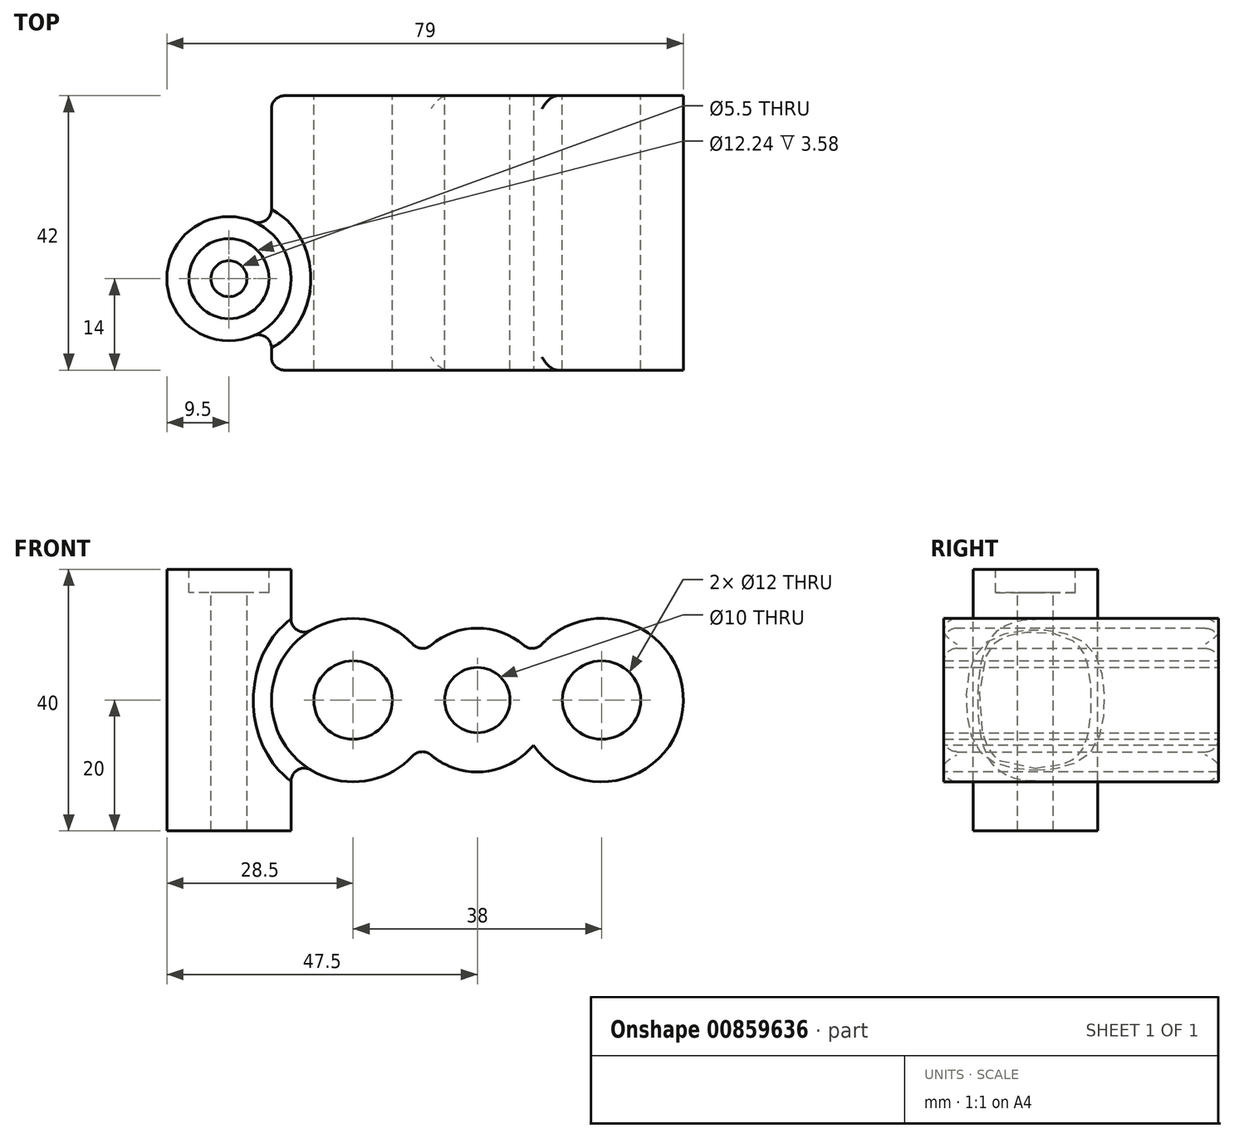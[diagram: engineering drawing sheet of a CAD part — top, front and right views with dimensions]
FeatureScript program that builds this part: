
annotation { "Feature Type Name" : "Feature", "Feature Type Description" : "" }
export const myFeature = defineFeature(function(context is Context, id is Id, definition is map)
    precondition{}
    {
        {
            var Q0;
            Q0=qCreatedBy(makeId("Top.planeOp"),FACE);
            var sketch = newSketch(context, id + "F0", { "sketchPlane" : qUnion([Q0])});
            skCircle(sketch, "E0", {"center": v(0, 0) * mm, "radius": 9.5 * mm});
            skSolve(sketch);
        }
        {
            var Q0;
            Q0 = qSketchRegion(id + "F0", true);
            extrude(context, id + "F1", {"entities" : qUnion([Q0]), "endBound" : BoundingType.SYMMETRIC, "oppositeDirection" : true, "depth" : 40 * mm, "offsetDistance" : 25 * mm});
        }
        {
            var Q0;
            Q0=qCreatedBy(makeId("Front.planeOp"),FACE);
            var sketch = newSketch(context, id + "F2", { "sketchPlane" : qUnion([Q0])});
            skArc(sketch, "E1", {"start": v(29.43, 6.9) * mm, "mid": v(6.5, 0) * mm, "end": v(29.43, -6.9) * mm});
            skArc(sketch, "E2", {"start": v(46.57, 6.9) * mm, "mid": v(38, 11) * mm, "end": v(29.43, 6.9) * mm});
            skArc(sketch, "E3", {"start": v(46.57, -6.9) * mm, "mid": v(69.5, 0) * mm, "end": v(46.57, 6.9) * mm});
            skArc(sketch, "E4.trimOffspring", {"start": v(29.43, -6.9) * mm, "mid": v(38, -11) * mm, "end": v(46.57, -6.9) * mm});
            skSolve(sketch);
        }
        {
            var Q0;
            Q0 = qSketchRegion(id + "F2", true);
            extrude(context, id + "F3", {"entities" : qUnion([Q0]), "operationType" : NewBodyOperationType.ADD, "oppositeDirection" : true, "depth" : (42 - 14) * mm, "offsetDistance" : 25 * mm, "hasSecondDirection" : true, "secondDirectionOppositeDirection" : false, "secondDirectionDepth" : 14 * mm});
        }
        {
            var Q0;
            Q0=makeQuery(id+"F1.opExtrude","CAP_FACE",FACE,{"disambiguationData":[OSD([sQuery(id+"F0.wireOp",EDGE,"E0")])],"isStart":true});
            var sketch = newSketch(context, id + "F4", { "sketchPlane" : qUnion([Q0])});
            skPoint(sketch, "E5", {"position": v(0, 0) * mm});
            skSolve(sketch);
        }
        {
            var Q0;
            Q0=sQuery(id+"F4.wireOp",VERTEX,"E5");
            var Q1;
            Q1=makeQuery(id+"F1.opExtrude","SWEPT_BODY",BODY,{"disambiguationData":[OSD([sQuery(id+"F0.wireOp",EDGE,"E0")])]});
            hole(context, id + "F5", {"style" : HoleStyle.C_BORE, "endStyle" : HoleEndStyle.THROUGH, "holeDiameter" : 5.5 * mm, "cBoreDiameter" : 12.24 * mm, "cBoreDepth" : 3.58 * mm, "majorDiameter" : 5 * mm, "isTappedThrough" : true, "tappedDepth" : 12 * mm, "tapClearance" : 3, "startFromSketch" : true, "locations" : qUnion([Q0]), "scope" : qUnion([Q1])});
        }
        {
            var Q0;
            Q0=makeQuery(id+"F3.opExtrude","CAP_FACE",FACE,{"disambiguationData":[OSD([sQuery(id+"F2.wireOp",EDGE,"E1"),sQuery(id+"F2.wireOp",EDGE,"E2"),sQuery(id+"F2.wireOp",EDGE,"E3"),sQuery(id+"F2.wireOp",EDGE,"E4.trimOffspring")])],"isStart":false});
            var sketch = newSketch(context, id + "F6", { "sketchPlane" : qUnion([Q0])});
            skPoint(sketch, "E6", {"position": v(-19, 0) * mm});
            skPoint(sketch, "E7", {"position": v(-38, 0) * mm});
            skPoint(sketch, "E8", {"position": v(-57, 0) * mm});
            skSolve(sketch);
        }
        {
            var Q0;
            Q0=sQuery(id+"F6.wireOp",VERTEX,"E6");
            var Q1;
            Q1=sQuery(id+"F6.wireOp",VERTEX,"E8");
            var Q2;
            Q2=makeQuery(id+"F1.opExtrude","SWEPT_BODY",BODY,{"disambiguationData":[OSD([sQuery(id+"F0.wireOp",EDGE,"E0")])]});
            hole(context, id + "F7", {"style" : HoleStyle.SIMPLE, "endStyle" : HoleEndStyle.THROUGH, "holeDiameter" : 12 * mm, "majorDiameter" : 5 * mm, "isTappedThrough" : true, "tappedDepth" : 12 * mm, "tapClearance" : 3, "startFromSketch" : true, "locations" : qUnion([Q0, Q1]), "scope" : qUnion([Q2])});
        }
        {
            var Q0;
            Q0=sQuery(id+"F6.wireOp",VERTEX,"E7");
            var Q1;
            Q1=makeQuery(id+"F1.opExtrude","SWEPT_BODY",BODY,{"disambiguationData":[OSD([sQuery(id+"F0.wireOp",EDGE,"E0")])]});
            hole(context, id + "F8", {"style" : HoleStyle.SIMPLE, "endStyle" : HoleEndStyle.THROUGH, "holeDiameter" : 10 * mm, "majorDiameter" : 5 * mm, "isTappedThrough" : true, "tappedDepth" : 12 * mm, "tapClearance" : 3, "startFromSketch" : true, "locations" : qUnion([Q0]), "scope" : qUnion([Q1])});
        }
        {
            var Q0;
            Q0=makeQuery(id+"F3.opExtrude","SWEPT_FACE",FACE,{"disambiguationData":[OSD([sQuery(id+"F2.wireOp",EDGE,"E2")])]});
            var Q1;
            Q1=makeQuery(id+"F3.opExtrude","SWEPT_FACE",FACE,{"disambiguationData":[OSD([sQuery(id+"F2.wireOp",EDGE,"E1")])]});
            fillet(context, id + "F9", {"entities" : qUnion([Q0, Q1]), "radius" : 2 * mm, "tangentPropagation" : true, "allowEdgeOverflow" : false});
        }
    });
